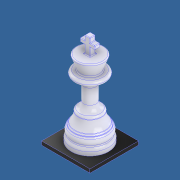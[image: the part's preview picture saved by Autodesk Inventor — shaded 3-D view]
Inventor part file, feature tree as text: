
AUTODESK INVENTOR PART (.ipt)
format: ipt  version: 2018 (Build 220112000, 112)  size: 386,560 bytes
history: native  units: in
note: dims shown in document units (in); Inventor stores cm internally (conversion verified against a paired STEP export)
features: fillet x14, extrude x11, sketch x11, chamfer x3, draft x1
ambient origin geometry x8: Origin, YZ Plane, XZ Plane, XY Plane, X Axis, Y Axis, Z Axis, Center Point
bodies: Solid1 (feature_tree)
feature tree (40):
  extrude  "Extrusion1"  Depth=0.1in TaperAngle=0.0deg
  fillet  "Fillet1"  Radius=0.1in
  extrude  "Extrusion2"  Depth=0.1in
  fillet  "Fillet2"  Radius=0.025in
  fillet  "Fillet3"  Radius=0.096in
  chamfer  "Chamfer1"  Distance=0.0625in
  extrude  "Extrusion3"  Depth=0.125in
  chamfer  "Chamfer2"  Distance=0.2835in
  fillet  "Fillet4"  Radius=0.375in
  fillet  "Fillet5"  Radius=0.0625in
  fillet  "Fillet6"  Radius=0.33in
  extrude  "Extrusion4"  Depth=0.1875in
  fillet  "Fillet7"  Radius=0.125in
  fillet  "Fillet8"  Radius=0.1875in
  extrude  "Extrusion5"  Depth=0.475in
  fillet  "Fillet9"  Radius=0.375in
  extrude  "Extrusion6"  Depth=0.148in
  fillet  "Fillet10"  Radius=0.4375in
  fillet  "Fillet11"  Radius=0.125in
  extrude  "Extrusion7"  Depth=0.1in TaperAngle=0.0deg
  draft  "FaceDraft1"
  extrude  "Extrusion8"  Depth=0.0225in
  extrude  "Extrusion9"  Depth=0.1in
  extrude  "Extrusion10"  Depth=0.1in TaperAngle=45.0deg
  fillet  "Fillet12"  Radius=1.3in
  fillet  "Fillet13"  Radius=1.3in
  fillet  "Fillet14"  Radius=0.65in
  chamfer  "Chamfer3"  Distance=0.65in
  extrude  "Extrusion11"  Depth=0.1in TaperAngle=0.0deg
  sketch  "Sketch1"  dims[d0=1.0in d1=0.2in d2=0.0in d3=0.1in]
  sketch  "Sketch2"  dims[d4=0.2in d5=0.0in d6=0.1in d7=0.025in]
  sketch  "Sketch3"  dims[d8=0.0625in d9=0.125in d10=0.3917in d11=0.096in d12=0.0in d13=0.0625in d14=0.125in d15=0.3779in]
  sketch  "Sketch4"  dims[d16=0.025in d17=0.125in]
  sketch  "Sketch5"  dims[d18=0.125in d19=0.2835in d20=0.0in d21=0.375in d22=0.0625in d23=0.33in]
  sketch  "Sketch6"  dims[d24=0.75in d25=0.0in d26=0.1875in d27=0.125in d28=0.0in d29=0.1875in]
  sketch  "Sketch7"  dims[d30=0.0625in d31=0.475in d32=0.375in d33=0.0in]
  sketch  "Sketch8"  dims[d34=-0.1374in d35=0.148in d36=0.4375in d37=0.0in d38=0.125in]
  sketch  "Sketch9"  dims[d39=0.1in d40=0.125in d41=0.0in]
  sketch  "Sketch10"  dims[d42=0.125in d43=0.0in d44=0.0225in]
  sketch  "Sketch11"  dims[d45=0.0225in d46=0.0225in d47=0.015in d48=0.125in d49=45.0deg d50=1.3in d51=1.3in d53=0.65in d54=0.65in d55=0.1in d56=0.0in]
